# Revit family: PRD_AR_Shlvs_MaximaShelfForCommercialSinks_MAXT
name_source: partatom
category: Plumbing Fixtures
revit_build: Autodesk Revit 2018 (Build: 20190510_1515(x64)
units: mm (PartAtom-declared; Revit-internal decimal feet)

## family parameters
Always vertical = Yes
Cut with Voids When Loaded = No
OmniClass Number = 23.40.20.00
OmniClass Title = General Furniture and Specialties
Part Type = Normal
Room Calculation Point = No
Round Connector Dimension = Use Diameter
Shared = Yes
Work Plane-Based = No

## types (12) — shared parameters
AssetType = Fixed
Category = Pr_40_30_78_19, Commercial kitchen shelving and racking units
Color = stainless steel
ConstructionShelvesEdges = all round
ConstructionShelvesFinish = satin finished
ConstructionShelvesMaterial = 1.2mm stainless steel 1.4301
ConstructionShelvesNumber = 1
ConstructionShelvesPositions = Fixed
CutLength2 = 44 mm  [stored 0.144357 ft]
DurationUnit = year
Features = stainless steel, surface satin finished, material thickness 1.2 mm, mounted on product
Finish = satin finished
IfcExportAs = IfcFurnitureType
IfcExportType = NOTDEFINED
MainColor = stainless steel
Manufacturer = KWC Group AG
ManufacturerName = KWC Group AG
ManufacturerURL = www.kwc.com
Material = stainless steel
NBSDescription = Stainless steel shelving and racking units
NBSReference = 45-35-15/462
NominalHeight = 41 mm  [stored 0.134514 ft]
OverallHeight = 41 mm  [stored 0.134514 ft]
ProductInformation = https://pim.kwc.com
Shape = Rectangular
Style = Shelf
TypeOfMounting = Mounted on product
URL = www.kwc.com
UnderframeMaterial = PRD_AR_StainlessSteel_SatinFinished
Uniclass2015Code = Pr_40_30_78_19
Uniclass2015Title = Commercial kitchen shelving and racking units
Uniclass2015Version = Products v1.10
Version = 1
WarrantyDurationUnit = year

## per-type parameters (varying)
| type | BIMObjectName | CutLength1 | CutLength3 | CutLength4 | Description | GrossWeight | ModelNumber | Name | NetWeight | NominalDepth | NominalWidth | OverallDepth | OverallWidth | Size |
| MAXT60-60 | PRD_AR_CommercialKitchenShelvingAndRackingUnits_MaximaShelfForCommercialSinks_MAXT60-60 | 44 mm  [stored 0.144357 ft] | 36 mm  [stored 0.11811 ft] | 44 mm  [stored 0.144357 ft] | Shelve for KWC commercial sinks, stainless steel, surface satin finished, material thickness 1.2 mm, incl. Shelve holder. for MAXS sinks (600 mm deep, 600 mm wide) | 4.00 kg | 2000057763 | Maxima shelve for sinks  width 600 mm / depth 600 mm | 4.00 kg | 548 mm | 586 mm  [stored 1.92257 ft] | 548 mm | 586 mm  [stored 1.92257 ft] | 586 x 548 x 41 mm |
| MAXT70-60 | PRD_AR_CommercialKitchenShelvingAndRackingUnits_MaximaShelfForCommercialSinks_MAXT70-60 | 44 mm  [stored 0.144357 ft] | 36 mm  [stored 0.11811 ft] | 44 mm  [stored 0.144357 ft] | Shelve for KWC commercial sinks, stainless steel, surface satin finished, material thickness 1.2 mm, incl. Shelve holder. for MAXS sinks (600 mm deep, 700 mm wide) | 4.50 kg | 2000100003 | Maxima shelve for sinks width 700 mm / depth 600 mm | 4.50 kg | 548 mm | 686 mm  [stored 2.25066 ft] | 548 mm | 686 mm  [stored 2.25066 ft] | 686 x 548 x 41 mm |
| MAXT70-70 | PRD_AR_CommercialKitchenShelvingAndRackingUnits_MaximaShelfForCommercialSinks_MAXT70-70 | 44 mm  [stored 0.144357 ft] | 36 mm  [stored 0.11811 ft] | 44 mm  [stored 0.144357 ft] | Shelve for KWC commercial sinks, stainless steel, surface satin finished, material thickness 1.2 mm, incl. Shelve holder. for MAXL sinks (700 mm deep, 700 mm wide) | 5.20 kg | 2000100002 | Maxima shelve for sinks width 700 mm / depth 700 mm | 5.20 kg | 648 mm  [stored 2.12598 ft] | 686 mm  [stored 2.25066 ft] | 648 mm  [stored 2.12598 ft] | 686 mm  [stored 2.25066 ft] | 686 x 648 x 41 mm |
| MAXT120-60 | PRD_AR_CommercialKitchenShelvingAndRackingUnits_MaximaShelfForCommercialSinks_MAXT120-60 | 44 mm  [stored 0.144357 ft] | 40 mm | 40 mm | Shelve for KWC commercial sinks, stainless steel, surface satin finished, material thickness 1.2 mm, incl. Shelve holder. for MAXS sinks (600 mm deep, 1200 mm wide) | 7.30 kg | 2000057716 | Maxima shelve for sinks width 1200 mm / depth 600 mm | 7.30 kg | 548 mm | 1186 mm | 548 mm | 1186 mm | 1186 x 548 x 41 mm |
| MAXT120-70 | PRD_AR_CommercialKitchenShelvingAndRackingUnits_MaximaShelfForCommercialSinks_MAXT120-70 | 44 mm  [stored 0.144357 ft] | 36 mm  [stored 0.11811 ft] | 44 mm  [stored 0.144357 ft] | Shelve for KWC commercial sinks, stainless steel, surface satin finished, material thickness 1.2 mm, incl. Shelve holder. for MAXL sinks (700 mm deep, 1200 mm wide) | 8.30 kg | 2000057755 | Maxima shelve for sinks width 1200 mm / depth 700 mm | 8.30 kg | 648 mm  [stored 2.12598 ft] | 1186 mm | 648 mm  [stored 2.12598 ft] | 1186 mm | 1186 x 648 x 41 mm |
| MAXT140-60 | PRD_AR_CommercialKitchenShelvingAndRackingUnits_MaximaShelfForCommercialSinks_MAXT140-60 | 44 mm  [stored 0.144357 ft] | 36 mm  [stored 0.11811 ft] | 44 mm  [stored 0.144357 ft] | Shelve for KWC commercial sinks, stainless steel, surface satin finished, material thickness 1.2 mm, incl. Shelve holder. for MAXS sinks (600 mm deep, 1400 mm wide) | 8.40 kg | 2000057756 | Maxima shelve for sinks  width 1400 mm / depth 600 mm | 8.40 kg | 548 mm | 1386 mm | 548 mm | 1386 mm | 1386 x 548 x 41 mm |
| MAXT140-70 | PRD_AR_CommercialKitchenShelvingAndRackingUnits_MaximaShelfForCommercialSinks_MAXT140-70 | 44 mm  [stored 0.144357 ft] | 36 mm  [stored 0.11811 ft] | 44 mm  [stored 0.144357 ft] | Shelve for KWC commercial sinks, stainless steel, surface satin finished, material thickness 1.2 mm, incl. Shelve holder. for MAXL sinks (700 mm deep, 1400 mm wide) | 9.60 kg | 2000057757 | Maxima shelve for sinks width 1400 mm / depth 700 mm | 9.60 kg | 648 mm  [stored 2.12598 ft] | 1386 mm | 648 mm  [stored 2.12598 ft] | 1386 mm | 1386 x 648 x 41 mm |
| MAXT160-60 | PRD_AR_CommercialKitchenShelvingAndRackingUnits_MaximaShelfForCommercialSinks_MAXT160-60 | 44 mm  [stored 0.144357 ft] | 36 mm  [stored 0.11811 ft] | 44 mm  [stored 0.144357 ft] | Shelve for KWC commercial sinks, stainless steel, surface satin finished, material thickness 1.2 mm, incl. Shelve holder. for MAXS sinks (600 mm deep, 1600 mm wide) | 9.50 kg | 2000057758 | Maxima shelve for sinks width 1600 mm / depth 600 mm | 9.50 kg | 548 mm | 1586 mm | 548 mm | 1586 mm | 1586 x 548 x 41 mm |
| MAXT200-60 | PRD_AR_CommercialKitchenShelvingAndRackingUnits_MaximaShelfForCommercialSinks_MAXT200-60 | 44 mm  [stored 0.144357 ft] | 36 mm  [stored 0.11811 ft] | 44 mm  [stored 0.144357 ft] | Shelve for KWC commercial sinks, stainless steel, surface satin finished, material thickness 1.2 mm, incl. Shelve holder. for MAXS sinks (600 mm deep, 2000 mm wide) | 13.90 kg | 2000057759 | Maxima shelve for sinks  width 2000 mm / depth 600 mm | 13.90 kg | 548 mm | 1986 mm | 548 mm | 1986 mm | 1986 x 548 x 41 mm |
| MAXT200-70 | PRD_AR_CommercialKitchenShelvingAndRackingUnits_MaximaShelfForCommercialSinks_MAXT200-70 | 44 mm  [stored 0.144357 ft] | 36 mm  [stored 0.11811 ft] | 44 mm  [stored 0.144357 ft] | Shelve for KWC commercial sinks, stainless steel, surface satin finished, material thickness 1.2 mm, incl. Shelve holder. for MAXL sinks (700 mm deep, 2000 mm wide) | 15.50 kg | 2000057760 | Maxima shelve for sinks width 2000 mm / depth 700 mm | 15.50 kg | 648 mm  [stored 2.12598 ft] | 1986 mm | 648 mm  [stored 2.12598 ft] | 1986 mm | 1986 x 648 x 41 mm |
| MAXT260-60 | PRD_AR_CommercialKitchenShelvingAndRackingUnits_MaximaShelfForCommercialSinks_MAXT260-60 | 21 mm | 36 mm  [stored 0.11811 ft] | 21 mm | Shelve for KWC commercial sinks, surface satin finished, material thickness 1.2 mm, incl. Shelve holder. for MAXS sinks (600 mm deep, 2600 mm wide) | 15.40 kg | 2000057761 | Maxima shelve for sinks  width 2600 mm / depth 600 mm | 15.40 kg | 548 mm | 2586 mm | 548 mm | 2586 mm | 2586 x 548 x 41 mm |
| MAXT260-70 | PRD_AR_CommercialKitchenShelvingAndRackingUnits_MaximaShelfForCommercialSinks_MAXT260-70 | 21 mm | 36 mm  [stored 0.11811 ft] | 21 mm | Shelve for KWC commercial sinks, stainless steel, surface satin finished, material thickness 1.2 mm, incl. Shelve holder. for MAXL sinks (700 mm deep, 2600 mm wide) | 18.50 kg | 2000100004 | Maxima shelve for sinks width 2600 mm / depth 700 mm | 18.50 kg | 648 mm  [stored 2.12598 ft] | 2586 mm | 648 mm  [stored 2.12598 ft] | 2586 mm | 2586 x 648 x 41 mm |

note: column(s) folded — value = type name in every type: Model, ModelReference

note: [stored X ft] marks values corroborated as IEEE doubles in the binary element streams (Revit-internal decimal feet)

## geometry (parser evidence)
native form markers: Sweep x3
no freeform markers — native parametric forms only
